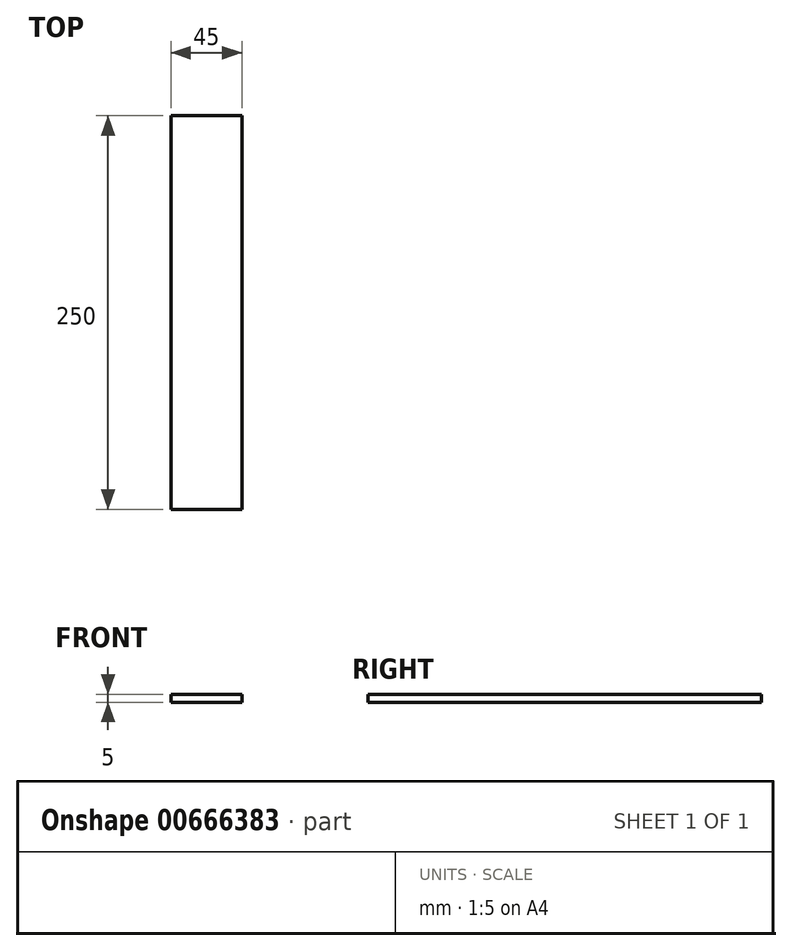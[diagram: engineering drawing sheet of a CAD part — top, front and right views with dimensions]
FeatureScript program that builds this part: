
annotation { "Feature Type Name" : "Feature", "Feature Type Description" : "" }
export const myFeature = defineFeature(function(context is Context, id is Id, definition is map)
    precondition{}
    {
        {
            var Q0;
            Q0=qCreatedBy(makeId("Top.planeOp"),FACE);
            var sketch = newSketch(context, id + "F0", { "sketchPlane" : qUnion([Q0])});
            skLineSegment(sketch, "E0.bottom", {"start": v(0, 0) * mm, "end": v(45, 0) * mm});
            skLineSegment(sketch, "E0.top", {"start": v(0, 250) * mm, "end": v(45, 250) * mm});
            skLineSegment(sketch, "E0.left", {"start": v(0, 0) * mm, "end": v(0, 250) * mm});
            skLineSegment(sketch, "E0.right", {"start": v(45, 0) * mm, "end": v(45, 250) * mm});
            skSolve(sketch);
        }
        {
            var Q0;
            Q0 = qSketchRegion(id + "F0", true);
            extrude(context, id + "F1", {"entities" : qUnion([Q0]), "depth" : 5 * mm, "offsetDistance" : 25 * mm});
        }
    });
